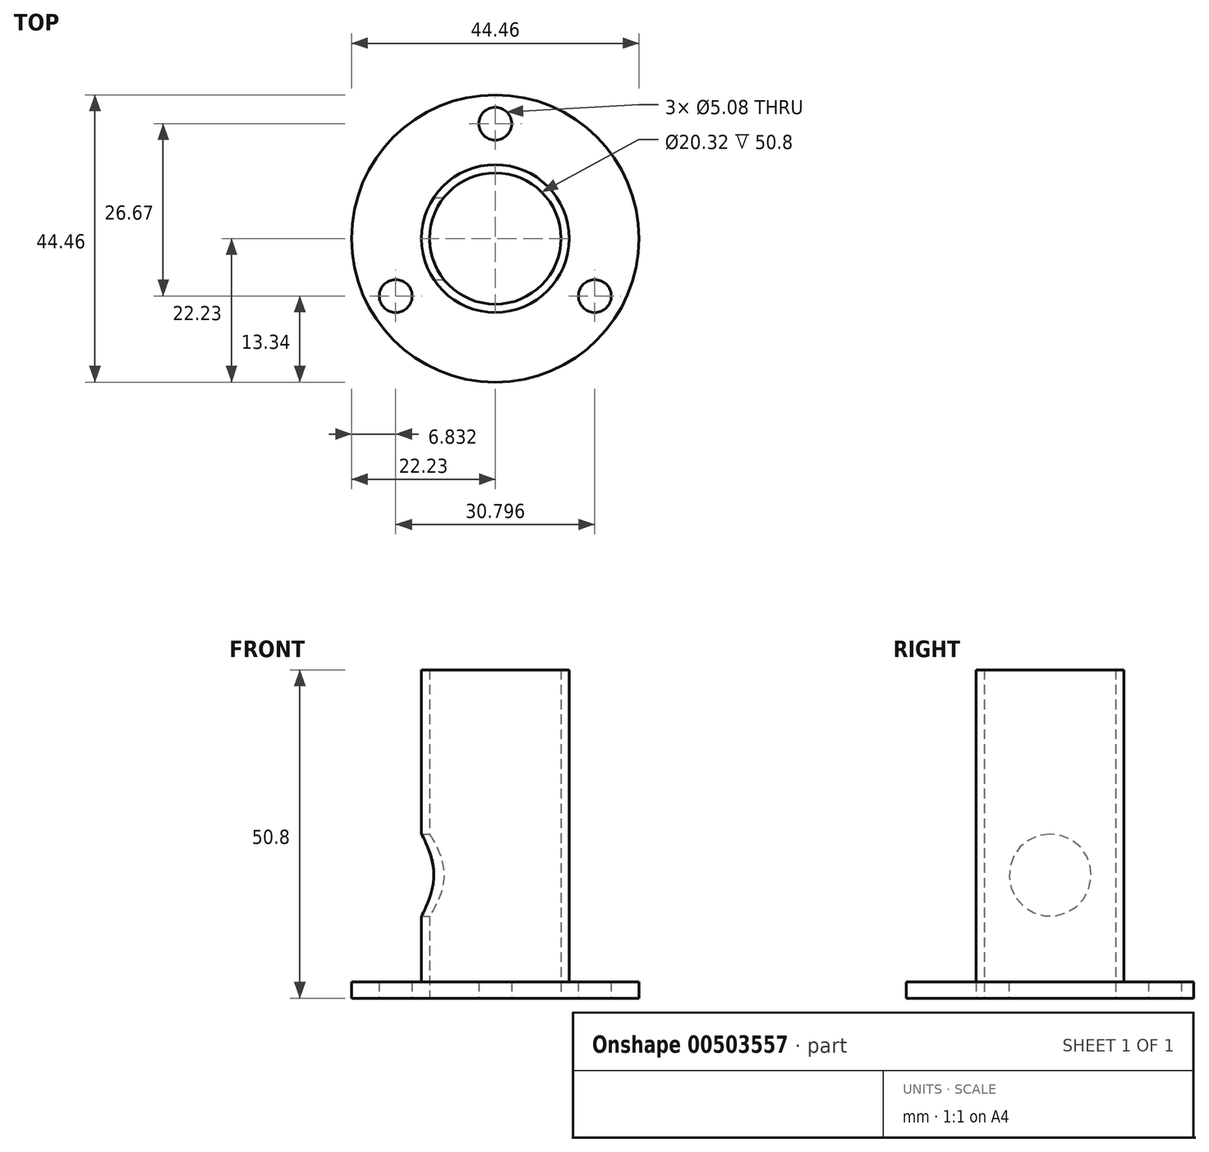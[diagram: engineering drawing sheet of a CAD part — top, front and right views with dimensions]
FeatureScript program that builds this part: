
annotation { "Feature Type Name" : "Feature", "Feature Type Description" : "" }
export const myFeature = defineFeature(function(context is Context, id is Id, definition is map)
    precondition{}
    {
        {
            var Q0;
            Q0=qCreatedBy(makeId("Top.planeOp"),FACE);
            var sketch = newSketch(context, id + "F0", { "sketchPlane" : qUnion([Q0])});
            skCircle(sketch, "E0", {"center": v(0, 0) * mm, "radius": 10.16 * mm});
            skCircle(sketch, "E1", {"center": v(0, 0) * mm, "radius": 22.23 * mm});
            skCircle(sketch, "E2", {"center": v(0, 17.78) * mm, "radius": 2.54 * mm});
            skCircle(sketch, "E3", {"center": v(15.4, -8.9) * mm, "radius": 2.54 * mm});
            skCircle(sketch, "E4", {"center": v(-15.4, -8.9) * mm, "radius": 2.54 * mm});
            skCircle(sketch, "E5", {"center": v(0, 0) * mm, "radius": 11.43 * mm});
            skSolve(sketch);
        }
        {
            var Q0;
            Q0=makeQuery(id+"F0.imprint","IMPRINT",FACE,{"disambiguationData":[TD([[makeQuery(id+"F0.imprint","IMPRINT",EDGE,{"derivedFrom":sQuery(id+"F0.wireOp",EDGE,"E0")}),-1.0]])]});
            extrude(context, id + "F1", {"entities" : qUnion([Q0]), "depth" : 50.8 * mm});
        }
        {
            var Q0;
            Q0 = qSketchRegion(id + "F0", true);
            extrude(context, id + "F2", {"entities" : qUnion([Q0]), "operationType" : NewBodyOperationType.ADD, "depth" : 2.54 * mm});
        }
        {
            var Q0;
            Q0=qCreatedBy(makeId("Right.planeOp"),FACE);
            var sketch = newSketch(context, id + "F3", { "sketchPlane" : qUnion([Q0])});
            skCircle(sketch, "E6", {"center": v(0, 19.05) * mm, "radius": 6.35 * mm});
            skSolve(sketch);
        }
        {
            var Q0;
            Q0 = qSketchRegion(id + "F3", true);
            extrude(context, id + "F4", {"entities" : qUnion([Q0]), "operationType" : NewBodyOperationType.REMOVE, "oppositeDirection" : true, "depth" : 12.7 * mm});
        }
    });
